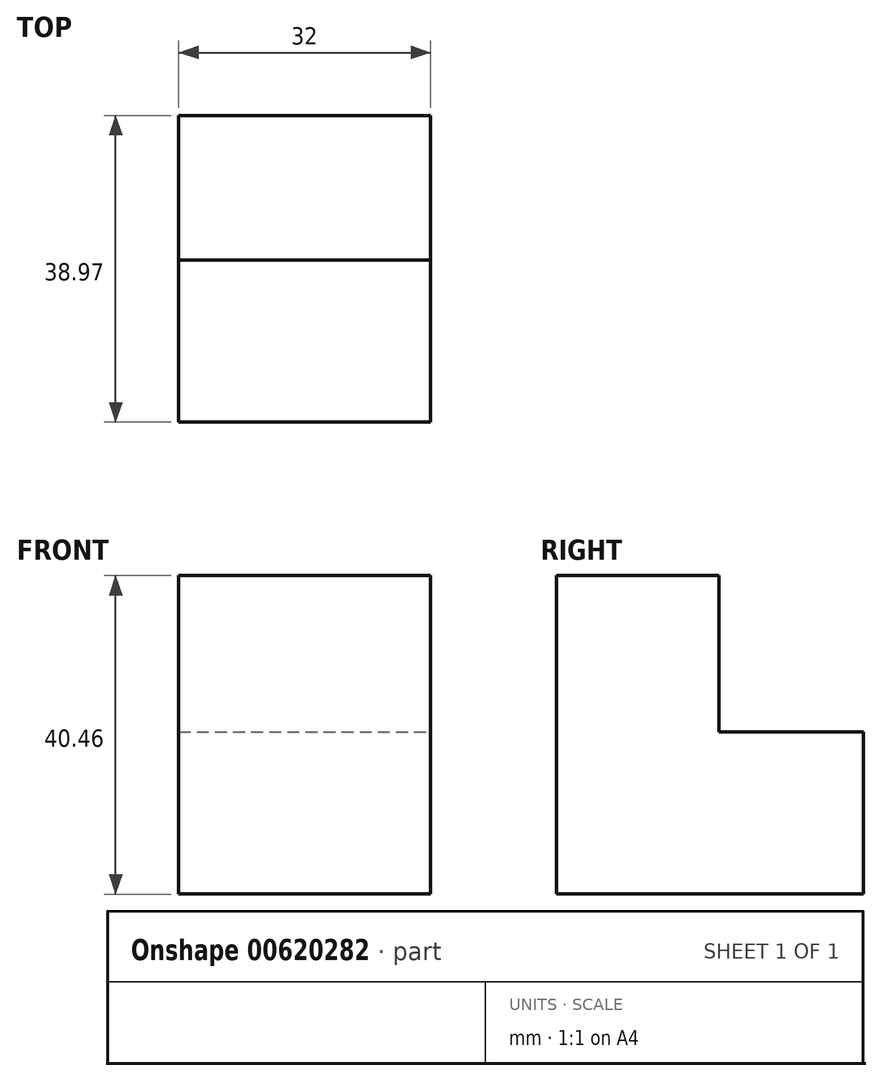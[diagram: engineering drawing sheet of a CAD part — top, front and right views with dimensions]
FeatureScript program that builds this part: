
annotation { "Feature Type Name" : "Feature", "Feature Type Description" : "" }
export const myFeature = defineFeature(function(context is Context, id is Id, definition is map)
    precondition{}
    {
        {
            var Q0;
            Q0=qCreatedBy(makeId("Right.planeOp"),FACE);
            var sketch = newSketch(context, id + "F0", { "sketchPlane" : qUnion([Q0])});
            skLineSegment(sketch, "E0", {"start": v(-48.68, 39.18) * mm, "end": v(-48.68, -1.28) * mm});
            skLineSegment(sketch, "E1", {"start": v(-48.68, -1.28) * mm, "end": v(-9.7, -1.28) * mm});
            skLineSegment(sketch, "E2", {"start": v(-9.7, -1.28) * mm, "end": v(-9.7, 19.32) * mm});
            skLineSegment(sketch, "E3", {"start": v(-9.7, 19.32) * mm, "end": v(-28.08, 19.32) * mm});
            skLineSegment(sketch, "E4", {"start": v(-28.08, 19.32) * mm, "end": v(-28.08, 39.18) * mm});
            skLineSegment(sketch, "E5", {"start": v(-28.08, 39.18) * mm, "end": v(-48.68, 39.18) * mm});
            skSolve(sketch);
        }
        {
            var Q0;
            Q0 = qSketchRegion(id + "F0", true);
            extrude(context, id + "F1", {"entities" : qUnion([Q0]), "oppositeDirection" : true, "depth" : 32 * mm, "offsetDistance" : 25 * mm});
        }
    });
